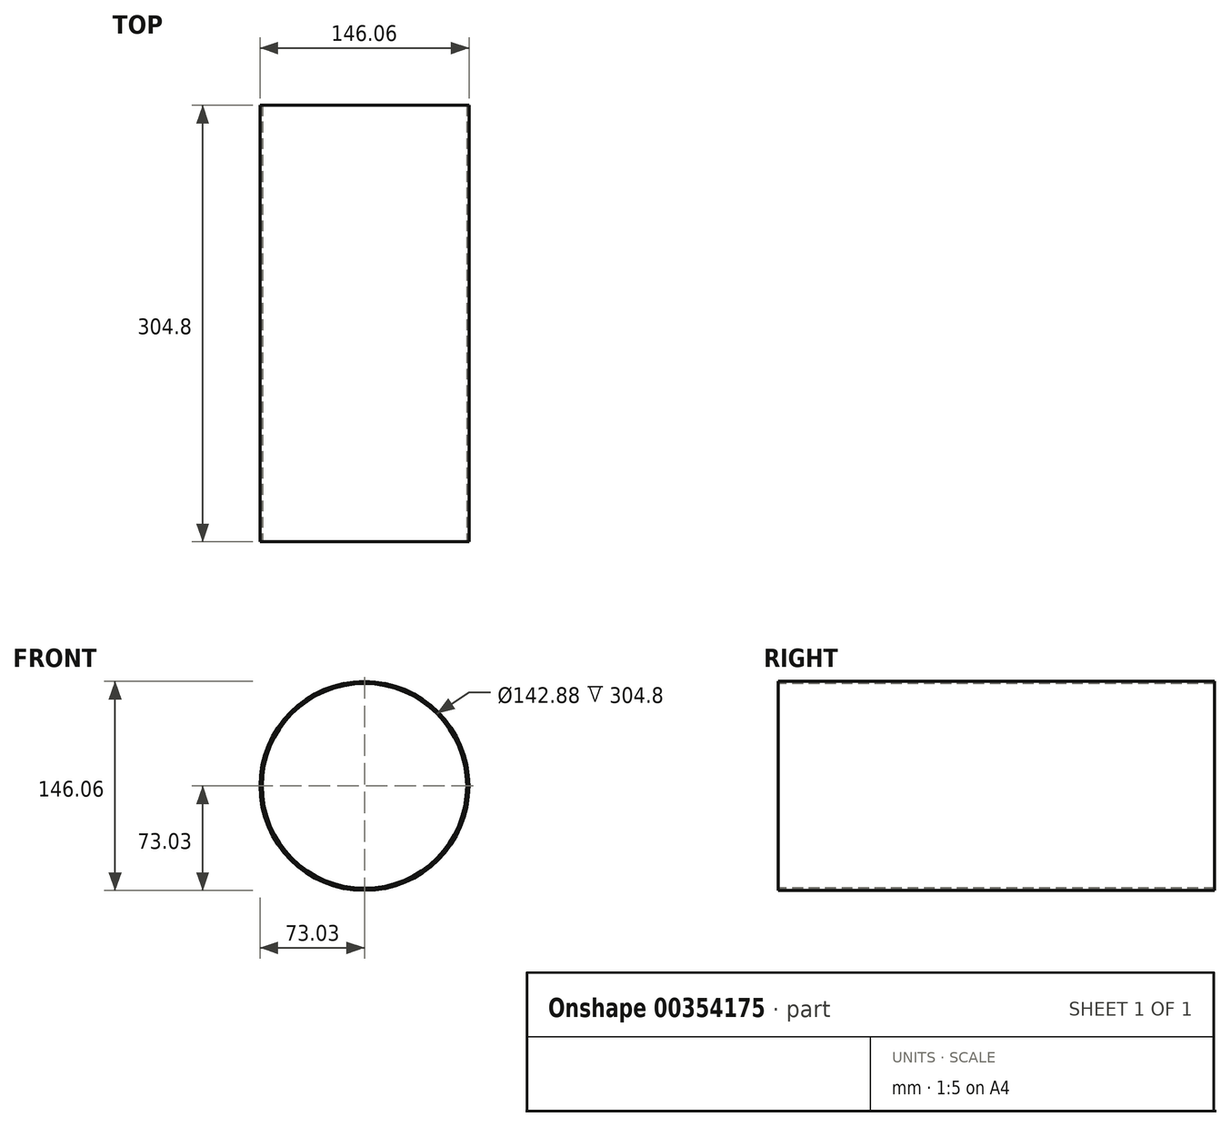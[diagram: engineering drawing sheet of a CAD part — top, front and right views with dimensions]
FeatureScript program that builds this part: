
annotation { "Feature Type Name" : "Feature", "Feature Type Description" : "" }
export const myFeature = defineFeature(function(context is Context, id is Id, definition is map)
    precondition{}
    {
        {
            var Q0;
            Q0=qCreatedBy(makeId("Front.planeOp"),FACE);
            var sketch = newSketch(context, id + "F0", { "sketchPlane" : qUnion([Q0])});
            skCircle(sketch, "E0", {"center": v(0, 0) * mm, "radius": 73.03 * mm});
            skCircle(sketch, "E1", {"center": v(0, 0) * mm, "radius": 71.44 * mm});
            skSolve(sketch);
        }
        {
            var Q0;
            Q0 = qSketchRegion(id + "F0", true);
            extrude(context, id + "F1", {"entities" : qUnion([Q0]), "oppositeDirection" : true, "depth" : 304.8 * mm});
        }
    });
